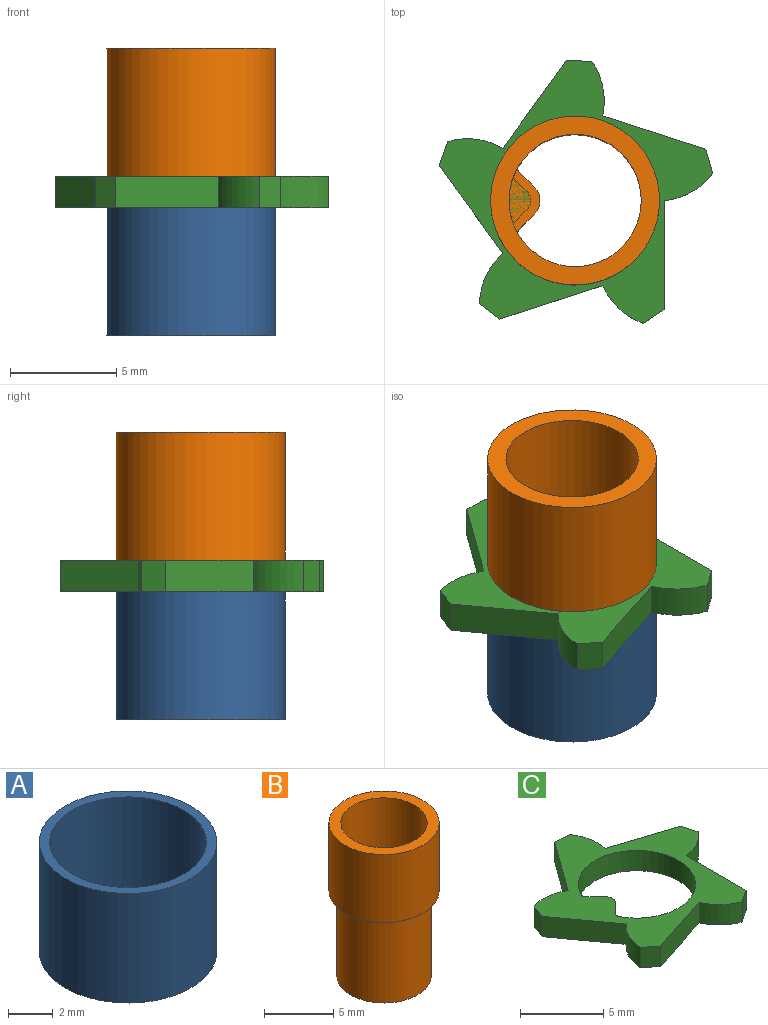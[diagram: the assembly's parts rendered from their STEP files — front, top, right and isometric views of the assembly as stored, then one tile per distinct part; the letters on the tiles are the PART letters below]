
ASSEMBLY  parts=3 mates=1
PART A: 4 faces, bbox 7.9x7.9x6 mm
  f0: cylinder r=3.51mm len=7.02mm, axis (0,0,-1), area 132.3mm2, adj f2,f3
  f1: cylinder r=3.97mm len=7.94mm, axis (0,0,-1), area 149.7mm2, adj f2,f3
  f2: plane 7.94x7.94mm, normal (0,0,1), area 10.8mm2, adj f0,f1
  f3: plane 7.94x7.94mm, normal (0,0,-1), area 10.8mm2, adj f0,f1
PART B: 12 faces, bbox 7.9x7.9x13.5 mm
  f0: cylinder r=3.11mm len=13.5mm, axis (0,0,-1), area 239mm2, adj f2,f4,f6,f7,f11
  f1: cylinder r=3.97mm len=7.94mm, axis (0,0,-1), area 149.7mm2, adj f2,f3
  f2: plane 7.94x7.94mm, normal (0,0,1), area 19.2mm2, adj f0,f1
  f3: plane 7.94x7.94mm, normal (0,0,-1), area 13.3mm2, adj f1,f10
  f4: plane 3.13x1.46mm, normal (0,0,1), area 2.7mm2, adj f0,f5,f6,f7,f8,f9
  f5: plane 7.5x0.75mm, normal (0.71,-0.71,0), area 7.9mm2, adj f4,f6,f9,f11
  f6: cylinder r=0.15mm len=7.5mm, axis (0,0,1), area 1.5mm2, adj f0,f4,f5,f11
  f7: cylinder r=0.15mm len=7.5mm, axis (0,0,1), area 1.5mm2, adj f0,f4,f8,f11
  f8: plane 7.5x0.75mm, normal (0.71,0.71,0), area 7.9mm2, adj f4,f7,f9,f11
  f9: cylinder r=0.9mm len=7.5mm, axis (0,0,1), area 10.6mm2, adj f4,f5,f8,f11
  f10: cylinder r=3.4mm len=7.5mm, axis (0,0,1), area 160mm2, adj f3,f11
  f11: plane 6.79x6.79mm, normal (0,0,-1), area 8.6mm2, adj f0,f5,f6,f7,f8,f9,f10
PART C: 23 faces, bbox 12.9x12.4x1.5 mm
  f0: plane 5.09x1.5mm, normal (1,0,0), area 7.6mm2, adj f1,f20,f21,f22
  f1: cylinder r=3.29mm len=2.28mm, axis (0,0,-1), area 4mm2, adj f0,f2,f21,f22
  f2: plane 1.5x1.15mm, normal (0.96,0.28,0), area 1.8mm2, adj f1,f3,f21,f22
  f3: plane 4.84x1.57mm, normal (0.31,0.95,0), area 7.6mm2, adj f2,f4,f21,f22
  f4: cylinder r=3.29mm len=2.56mm, axis (0,0,-1), area 4mm2, adj f3,f5,f21,f22
  f5: plane 1.5x1.2mm, normal (0.03,1,0), area 1.8mm2, adj f4,f6,f21,f22
  f6: plane 4.12x2.99mm, normal (-0.81,0.59,0), area 7.6mm2, adj f5,f7,f21,f22
  f7: cylinder r=3.29mm len=2.59mm, axis (0,0,-1), area 4mm2, adj f6,f8,f21,f22
  f8: plane 1.5x1.13mm, normal (-0.94,0.34,0), area 1.8mm2, adj f7,f9,f21,f22
  f9: plane 4.12x2.99mm, normal (-0.81,-0.59,0), area 7.6mm2, adj f8,f10,f21,f22
  f10: cylinder r=3.29mm len=2.37mm, axis (0,0,-1), area 4mm2, adj f9,f11,f21,f22
  f11: plane 1.5x0.95mm, normal (-0.61,-0.79,0), area 1.8mm2, adj f10,f12,f21,f22
  f12: plane 4.84x1.57mm, normal (0.31,-0.95,0), area 7.6mm2, adj f11,f13,f21,f22
  f13: cylinder r=3.29mm len=1.91mm, axis (0,0,-1), area 4mm2, adj f12,f20,f21,f22
  f14: cylinder r=3.53mm len=7.06mm, axis (0,0,-1), area 28.3mm2, adj f15,f19,f21,f22
  f15: cylinder r=0.3mm len=1.5mm, axis (0,0,-1), area 0.6mm2, adj f14,f16,f21,f22
  f16: plane 1.5x0.83mm, normal (0.71,-0.71,0), area 1.8mm2, adj f15,f17,f21,f22
  f17: cylinder r=0.6mm len=1.5mm, axis (0,0,-1), area 1.4mm2, adj f16,f18,f21,f22
  f18: plane 1.5x0.83mm, normal (0.71,0.71,0), area 1.8mm2, adj f17,f19,f21,f22
  f19: cylinder r=0.3mm len=1.5mm, axis (0,0,-1), area 0.6mm2, adj f14,f18,f21,f22
  f20: plane 1.5x0.99mm, normal (0.56,-0.83,0), area 1.8mm2, adj f0,f13,f21,f22
  f21: plane 12.87x12.36mm, normal (0,0,1), area 52.2mm2, adj f0,f1,f2,f3,f4,f5,f6,f7
  f22: plane 12.87x12.36mm, normal (0,0,-1), area 52.2mm2, adj f0,f1,f2,f3,f4,f5,f6,f7
PLACE A t=(0,0,-6.5)mm
PLACE B t=(0,0,1)mm
PLACE C t=(0,0,-0.5)mm
MATE fastened C.f14 <-> A.f0  axis (0,0,-1) through (0,0,-0.5)mm
